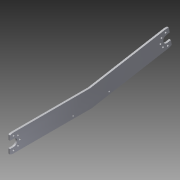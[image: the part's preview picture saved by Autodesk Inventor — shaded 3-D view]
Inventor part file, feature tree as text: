
AUTODESK INVENTOR PART (.ipt)
format: ipt  version: 2013 (Build 170138000, 138)  size: 2,846,208 bytes
history: native  units: mm
features: sketch x10, hole x6, extrude x4, other x2, pattern_circular x2, fillet x1
ambient origin geometry x8: Origin, YZ Plane, XZ Plane, XY Plane, X Axis, Y Axis, Z Axis, Center Point
feature tree (25):
  other  "ソリッド1"
  extrude  "押し出し1"  Depth=20.0mm
  hole  "穴2"  [1 undecoded]
  extrude  "押し出し2"  Depth=10.0mm
  hole  "穴3"  [1 undecoded]
  hole  "穴4"  [1 undecoded]
  pattern_circular  "円形状パターン3"  [2 undecoded]
  hole  "穴5"  [1 undecoded]
  hole  "穴6"  [1 undecoded]
  extrude  "押し出し4"  Depth=4.0mm
  fillet  "フィレット1"  Radius=170.0mm
  extrude  "押し出し5"  Depth=2.0mm TaperAngle=0.0deg
  hole  "穴7"  [1 undecoded]
  pattern_circular  "円形状パターン4"  Count=4  [1 undecoded]
  sketch  "スケッチ2"
  sketch  "スケッチ4"
  sketch  "スケッチ5"
  sketch  "スケッチ6"
  sketch  "スケッチ7"
  sketch  "スケッチ8"
  sketch  "スケッチ11"
  sketch  "スケッチ13"
  sketch  "スケッチ14"
  sketch  "スケッチ15"
  other  "断面エッジを投影1"
note: 9 required parameter values undecoded (feature->parameter linkage not recoverable at this tier; creation-order binding heuristic only, values carry confidence <= 0.55)
